# Revit family: VERTICAL 120 FLUSH PANEL ELAM FRAME BACK MOTOR)
name_source: partatom
category: Generic Models
revit_build: Autodesk Revit 2018 (Build: 20190510_1515(x64)
units: mm (PartAtom-declared; Revit-internal decimal feet)

## family parameters
Always vertical = Yes
Can host rebar = No
Cut with Voids When Loaded = No
Part Type = Normal
Room Calculation Point = No
Round Connector Dimension = Use Diameter
Shared = No
Work Plane-Based = No

## types (1)
- VERTICAL 120 FLUSH PANEL ELAM FRAME BACK MOTOR)
    120 LOUVREBLADE WEATHERBOARD = SILVER STAR
    BASE PLATE = STEEL MATERIAL
    BASE PLATE HOLE DIAMETER = 8 mm  [stored 0.0262467 ft]
    BASE PLATE HOLE SPACING HORIZONTAL = 120 mm  [stored 0.393701 ft]
    BASE PLATE HOLE VERTICAL = 70 mm  [stored 0.229659 ft]
    BASE PLATE LENGTH = 150 mm
    BASE PLATE THICKNESS = 5 mm  [stored 0.0164042 ft]
    BASE PLATE WIDTH = 100 mm  [stored 0.328084 ft]
    DRIVE BEARING = STEEL MATERIAL
    END CAP = SILVER STAR
    FRAMING = LIGHT BLUE GRAY
    HEIGHT = 2000 mm  [stored 6.56168 ft]
    LEG = STEEL MATERIAL
    LEG 1 = Yes
    LEG 2 = Yes
    LEG LENGTH = 200 mm  [stored 0.656168 ft]
    LOUVRE ANGLE = 45.00°
    MOTOR COVER = LIGHT BLUE GRAY
    MOTOR LENGTH = 800 mm  [stored 2.62467 ft]
    SPACING = 115 mm  [stored 0.377297 ft]
    WIDTH = 1500 mm  [stored 4.92126 ft]

note: [stored X ft] marks values corroborated as IEEE doubles in the binary element streams (Revit-internal decimal feet)

## geometry (parser evidence)
native form markers: Sweep x25
no freeform markers — native parametric forms only
